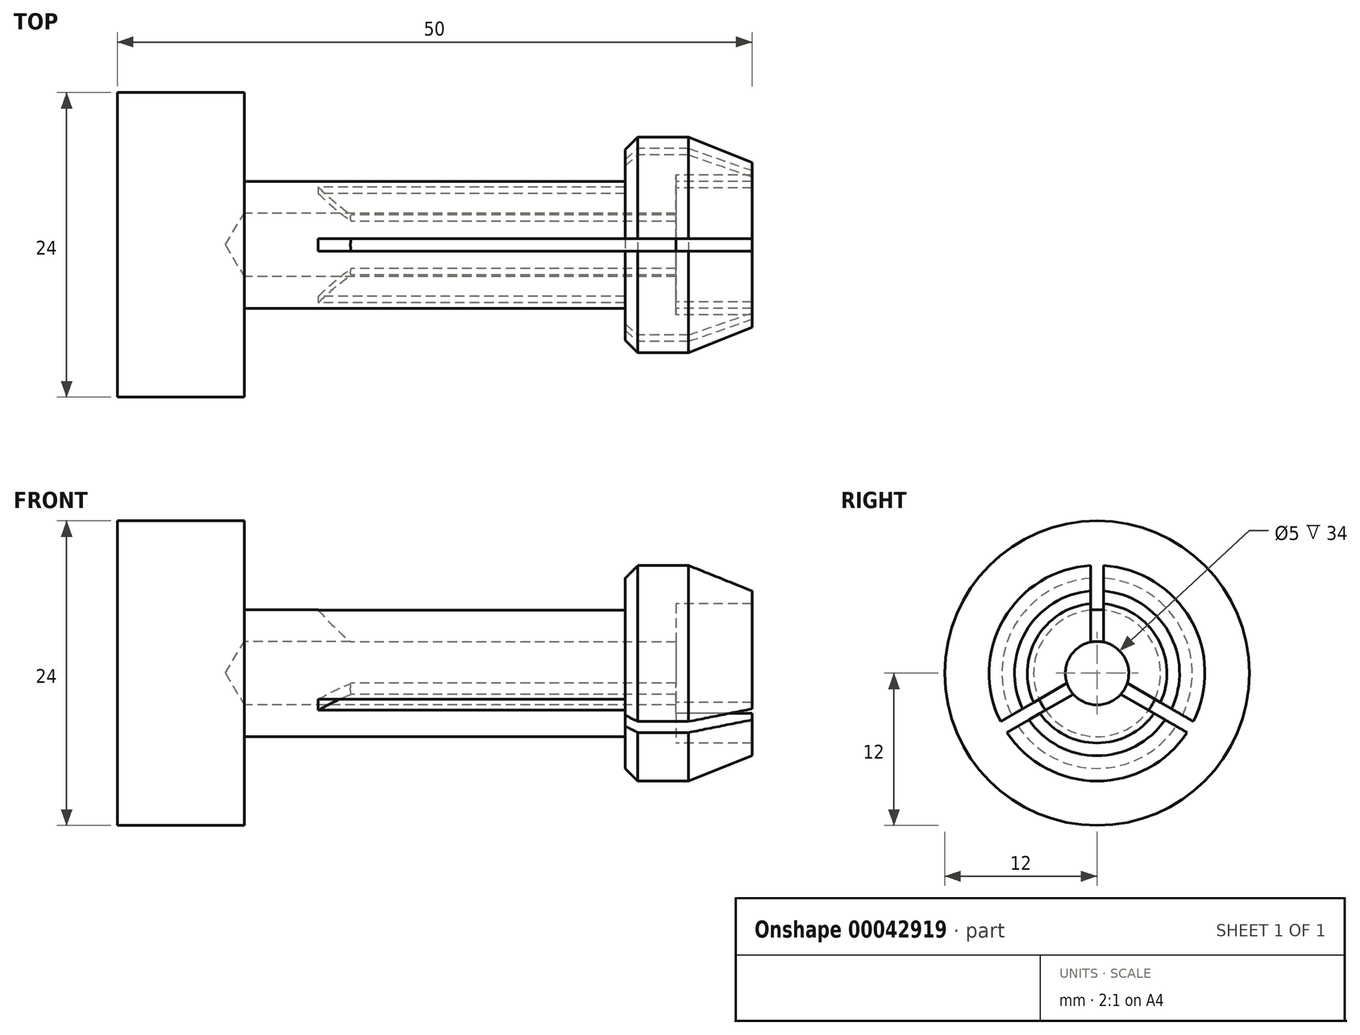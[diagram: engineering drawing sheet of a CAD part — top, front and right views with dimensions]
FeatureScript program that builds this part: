
annotation { "Feature Type Name" : "Feature", "Feature Type Description" : "" }
export const myFeature = defineFeature(function(context is Context, id is Id, definition is map)
    precondition{}
    {
        {
            var Q0;
            Q0=qCreatedBy(makeId("Front.planeOp"),FACE);
            var sketch = newSketch(context, id + "F0", { "sketchPlane" : qUnion([Q0])});
            skLineSegment(sketch, "E0", {"start": v(10, 5) * mm, "end": v(40, 5) * mm});
            skLineSegment(sketch, "E1", {"start": v(40, 5) * mm, "end": v(40, 8.5) * mm});
            skLineSegment(sketch, "E2", {"start": v(40, 8.5) * mm, "end": v(45, 8.5) * mm});
            skLineSegment(sketch, "E3", {"start": v(50, 6.5) * mm, "end": v(50, 5.5) * mm});
            skLineSegment(sketch, "E4", {"start": v(50, 5.5) * mm, "end": v(44, 5.5) * mm});
            skLineSegment(sketch, "E5", {"start": v(44, 5.5) * mm, "end": v(44, 2.5) * mm});
            skLineSegment(sketch, "E6", {"start": v(44, 2.5) * mm, "end": v(10, 2.5) * mm});
            skLineSegment(sketch, "E7", {"start": v(45, 8.5) * mm, "end": v(50, 6.5) * mm});
            skLineSegment(sketch, "E8", {"start": v(10, 5) * mm, "end": v(10, 12) * mm});
            skLineSegment(sketch, "E9", {"start": v(10, 12) * mm, "end": v(0, 12) * mm});
            skLineSegment(sketch, "E10", {"start": v(0, 12) * mm, "end": v(0, 0) * mm});
            skLineSegment(sketch, "E11", {"start": v(0, 0) * mm, "end": v(8.5, 0) * mm});
            skLineSegment(sketch, "E12", {"start": v(10, 2.5) * mm, "end": v(8.5, 0) * mm});
            skSolve(sketch);
        }
        {
            var Q0;
            Q0=makeQuery(id+"F0.imprint","IMPRINT",FACE,{"disambiguationData":[TD([[makeQuery(id+"F0.imprint","IMPRINT",EDGE,{"derivedFrom":sQuery(id+"F0.wireOp",EDGE,"E0")}),-1.0]])]});
            var Q1;
            Q1=sQuery(id+"F0.wireOp",EDGE,"E11");
            revolve(context, id + "F1", {"entities" : qUnion([Q0]), "axis" : qUnion([Q1]), "revolveType" : RevolveType.FULL});
        }
        {
            var Q0;
            Q0=makeQuery(id+"F1.opRevolve","SWEPT_EDGE",EDGE,{"disambiguationData":[OSD([sQuery(id+"F0.wireOp",EDGE,"E1"),sQuery(id+"F0.wireOp",EDGE,"E2")])]});
            chamfer(context, id + "F2", {"entities" : qUnion([Q0]), "width" : 1 * mm, "tangentPropagation" : true});
        }
        {
            var Q0;
            Q0=qCreatedBy(makeId("Front.planeOp"),FACE);
            var sketch = newSketch(context, id + "F3", { "sketchPlane" : qUnion([Q0])});
            skArc(sketch, "E13", {"start": v(31, 38) * mm, "mid": v(11, 18) * mm, "end": v(31, -2) * mm});
            skLineSegment(sketch, "E14", {"start": v(0, 0) * mm, "end": v(124.91, 0) * mm, "construction": true});
            skLineSegment(sketch, "E15", {"start": v(31, -2) * mm, "end": v(56.2, -2) * mm});
            skLineSegment(sketch, "E16", {"start": v(56.2, -2) * mm, "end": v(56.2, 38) * mm});
            skLineSegment(sketch, "E17", {"start": v(56.2, 38) * mm, "end": v(31, 38) * mm});
            skSolve(sketch);
        }
        {
            var Q0;
            Q0=makeQuery(id+"F3.imprint","IMPRINT",FACE,{"disambiguationData":[TD([[makeQuery(id+"F3.imprint","IMPRINT",EDGE,{"derivedFrom":sQuery(id+"F3.wireOp",EDGE,"E13")}),1.0]])]});
            extrude(context, id + "F4", {"entities" : qUnion([Q0]), "endBound" : BoundingType.SYMMETRIC, "depth" : 1 * mm});
        }
        {
            var Q0;
            Q0=makeQuery(id+"F4.opExtrude","SWEPT_BODY",BODY,{"disambiguationData":[OSD([sQuery(id+"F3.wireOp",EDGE,"E13"),sQuery(id+"F3.wireOp",EDGE,"E15"),sQuery(id+"F3.wireOp",EDGE,"E16"),sQuery(id+"F3.wireOp",EDGE,"E17")])]});
            var Q1;
            Q1=sQuery(id+"F3.wireOp",EDGE,"E14");
            circularPattern(context, id + "F5", {"entities" : qUnion([Q0]), "axis" : qUnion([Q1]), "angle" : 360 * degree, "instanceCount" : round(3), "equalSpace" : true});
        }
        {
            var Q0;
            Q0=makeQuery(id+"F4.opExtrude","SWEPT_BODY",BODY,{"disambiguationData":[OSD([sQuery(id+"F3.wireOp",EDGE,"E13"),sQuery(id+"F3.wireOp",EDGE,"E15"),sQuery(id+"F3.wireOp",EDGE,"E16"),sQuery(id+"F3.wireOp",EDGE,"E17")])]});
            var Q1;
            Q1=makeQuery(id+"F5.opPattern","COPY",BODY,{"derivedFrom":makeQuery(id+"F4.opExtrude","SWEPT_BODY",BODY,{"disambiguationData":[OSD([sQuery(id+"F3.wireOp",EDGE,"E13"),sQuery(id+"F3.wireOp",EDGE,"E15"),sQuery(id+"F3.wireOp",EDGE,"E16"),sQuery(id+"F3.wireOp",EDGE,"E17")])]}),"instanceName":"1"});
            var Q2;
            Q2=makeQuery(id+"F5.opPattern","COPY",BODY,{"derivedFrom":makeQuery(id+"F4.opExtrude","SWEPT_BODY",BODY,{"disambiguationData":[OSD([sQuery(id+"F3.wireOp",EDGE,"E13"),sQuery(id+"F3.wireOp",EDGE,"E15"),sQuery(id+"F3.wireOp",EDGE,"E16"),sQuery(id+"F3.wireOp",EDGE,"E17")])]}),"instanceName":"2"});
            var Q3;
            Q3=makeQuery(id+"F1.opRevolve","SWEPT_BODY",BODY,{"disambiguationData":[OSD([sQuery(id+"F0.wireOp",EDGE,"f868a5a4-03d5-4aa1-a47b-474d7ef3e890"),sQuery(id+"F0.wireOp",EDGE,"E0"),sQuery(id+"F0.wireOp",EDGE,"E1"),sQuery(id+"F0.wireOp",EDGE,"E2"),sQuery(id+"F0.wireOp",EDGE,"E3"),sQuery(id+"F0.wireOp",EDGE,"E4"),sQuery(id+"F0.wireOp",EDGE,"E5"),sQuery(id+"F0.wireOp",EDGE,"E6"),sQuery(id+"F0.wireOp",EDGE,"E7")])]});
            booleanBodies(context, id + "F6", {"operationType" : BooleanOperationType.SUBTRACTION, "tools" : qUnion([Q0, Q1, Q2]), "targets" : qUnion([Q3])});
        }
    });
